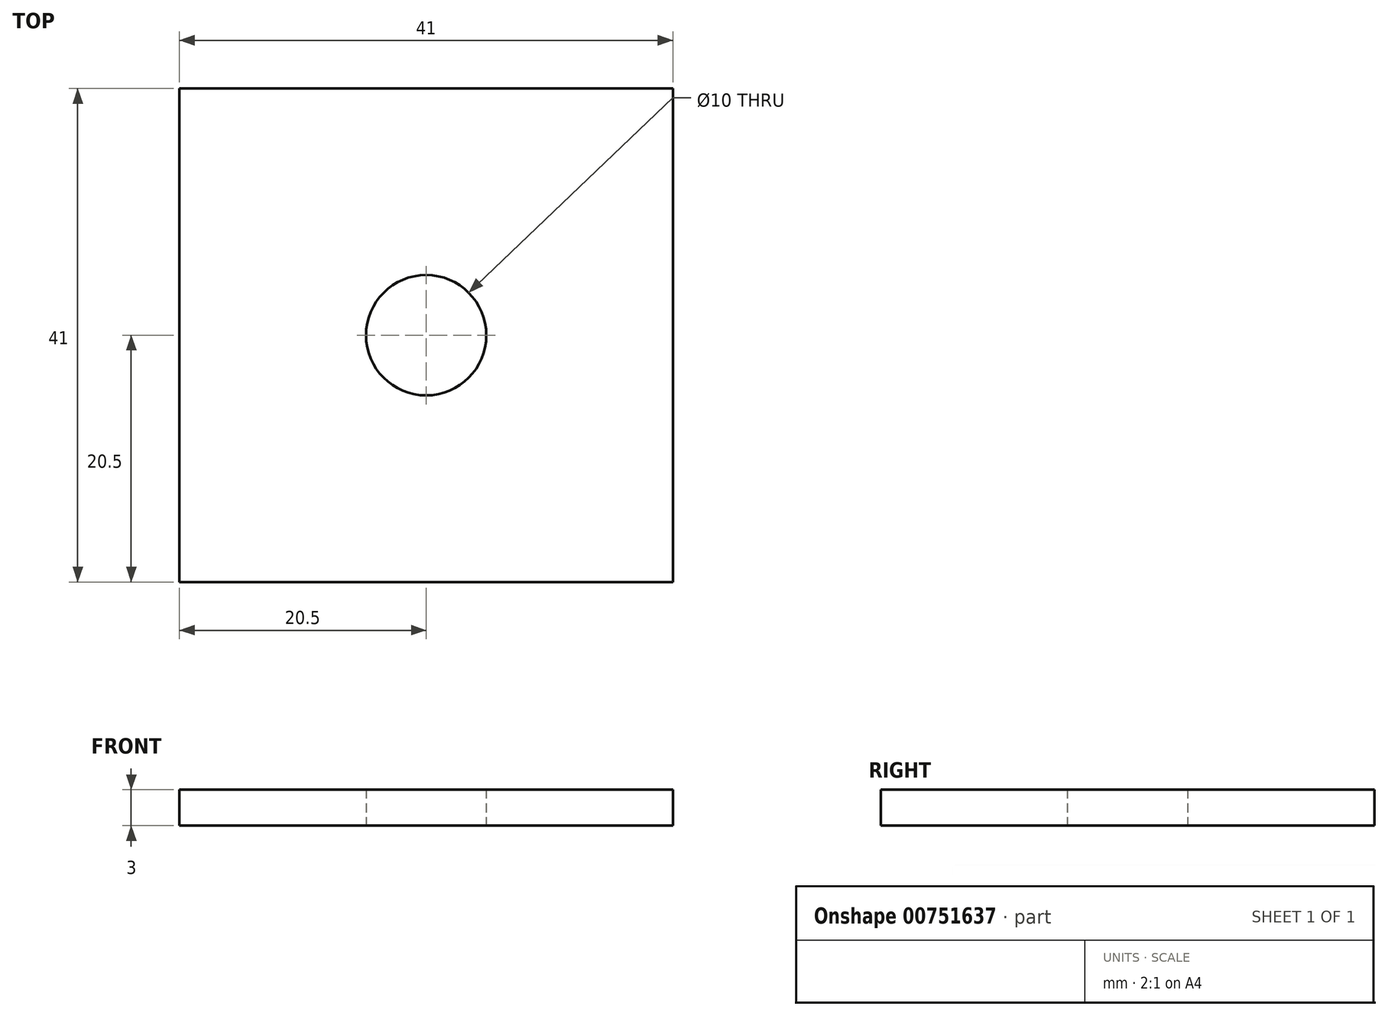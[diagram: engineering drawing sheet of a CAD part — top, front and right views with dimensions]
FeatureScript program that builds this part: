
annotation { "Feature Type Name" : "Feature", "Feature Type Description" : "" }
export const myFeature = defineFeature(function(context is Context, id is Id, definition is map)
    precondition{}
    {
        {
            var Q0;
            Q0=qCreatedBy(makeId("Top.planeOp"),FACE);
            var sketch = newSketch(context, id + "F0", { "sketchPlane" : qUnion([Q0])});
            skLineSegment(sketch, "E0.bottom", {"start": v(0, 0) * mm, "end": v(41, 0) * mm});
            skLineSegment(sketch, "E0.top", {"start": v(0, 41) * mm, "end": v(41, 41) * mm});
            skLineSegment(sketch, "E0.left", {"start": v(0, 0) * mm, "end": v(0, 41) * mm});
            skLineSegment(sketch, "E0.right", {"start": v(41, 0) * mm, "end": v(41, 41) * mm});
            skCircle(sketch, "E1", {"center": v(20.5, 20.5) * mm, "radius": 5 * mm});
            skPoint(sketch, "E1.centerSnap0", {"position": v(41, 20.5) * mm});
            skPoint(sketch, "E1.centerSnap1", {"position": v(20.5, 41) * mm});
            skSolve(sketch);
        }
        {
            var Q0;
            Q0=qSketchRegion(id+"F0",true);
            extrude(context, id + "F1", {"entities" : qUnion([Q0]), "depth" : 3 * mm});
        }
    });
